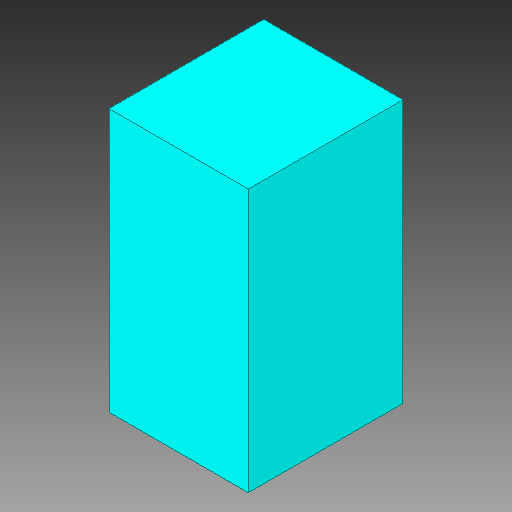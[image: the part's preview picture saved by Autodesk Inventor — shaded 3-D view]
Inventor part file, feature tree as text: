
AUTODESK INVENTOR PART (.ipt)
format: ipt  version: 2018 (Build 220112000, 112)  size: 80,896 bytes
history: native  units: in
note: dims shown in document units (in); Inventor stores cm internally (conversion verified against a paired STEP export)
features: other x1, extrude x1
ambient origin geometry x8: Origin, YZ Plane, XZ Plane, XY Plane, X Axis, Y Axis, Z Axis, Center Point
bodies: Solid1 (feature_tree)
feature tree (2):
  other  "CHIP-LED0603, CHIP-LED0603_86"
  extrude  "Extrusion1"  Depth=0.0394in TaperAngle=0.0deg
